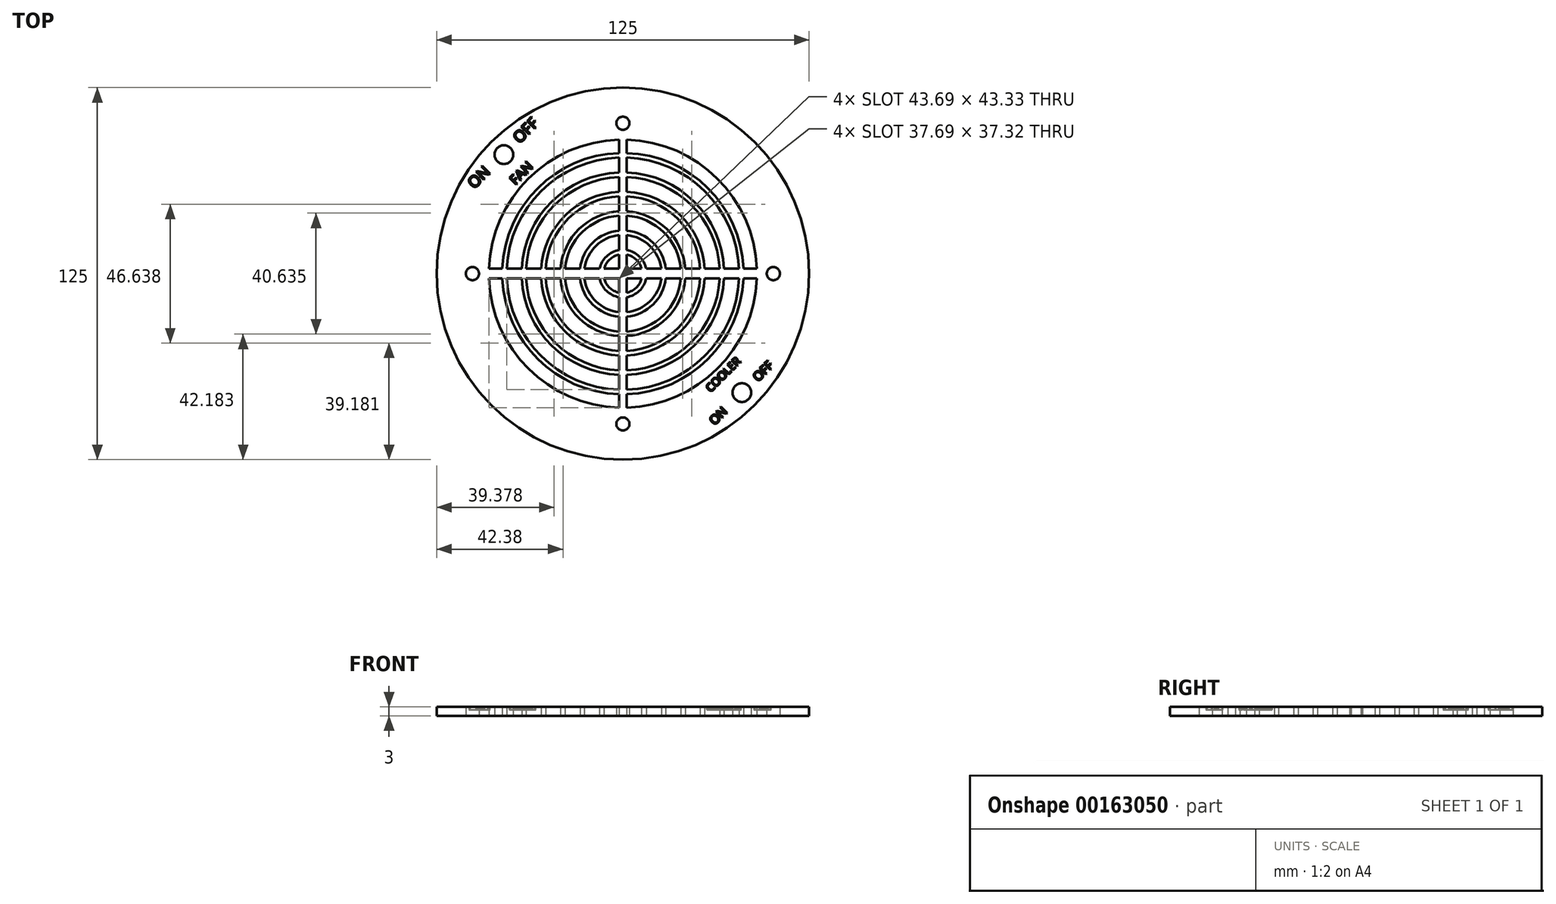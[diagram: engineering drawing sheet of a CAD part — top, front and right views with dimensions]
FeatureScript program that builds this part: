
annotation { "Feature Type Name" : "Feature", "Feature Type Description" : "" }
export const myFeature = defineFeature(function(context is Context, id is Id, definition is map)
    precondition{}
    {
        {
            var Q0;
            Q0=qCreatedBy(makeId("Top.planeOp"),FACE);
            var sketch = newSketch(context, id + "F0", { "sketchPlane" : qUnion([Q0])});
            skArc(sketch, "E0", {"start": v(-44.97, -1.66) * mm, "mid": v(-31.68, -31.95) * mm, "end": v(-1.28, -44.98) * mm});
            skCircle(sketch, "E1", {"center": v(0, 0) * mm, "radius": 62.5 * mm});
            skCircle(sketch, "E2", {"center": v(0, 0) * mm, "radius": 50.5 * mm, "construction": true});
            skPoint(sketch, "E3.center.orphan", {"position": v(-50.5, 0) * mm});
            skPoint(sketch, "E4.center", {"position": v(0.42, -0.72) * mm});
            skPoint(sketch, "E5.start.orphan", {"position": v(0, 45) * mm});
            skPoint(sketch, "E6.start.orphan", {"position": v(0, -45) * mm});
            skPoint(sketch, "E7.orphan", {"position": v(-45, 0) * mm});
            skArc(sketch, "E8", {"start": v(-6.29, -1.66) * mm, "mid": v(-4.46, -4.73) * mm, "end": v(-1.28, -6.37) * mm});
            skArc(sketch, "E9", {"start": v(-7.83, -1.66) * mm, "mid": v(-5.52, -5.8) * mm, "end": v(-1.28, -7.9) * mm});
            skArc(sketch, "E10", {"start": v(-12.9, -1.66) * mm, "mid": v(-9.06, -9.33) * mm, "end": v(-1.28, -12.94) * mm});
            skArc(sketch, "E11", {"start": v(-14.4, -1.66) * mm, "mid": v(-10.12, -10.39) * mm, "end": v(-1.28, -14.44) * mm});
            skArc(sketch, "E12", {"start": v(-19.43, -1.66) * mm, "mid": v(-13.65, -13.92) * mm, "end": v(-1.28, -19.46) * mm});
            skArc(sketch, "E13", {"start": v(-20.93, -1.66) * mm, "mid": v(-14.71, -14.98) * mm, "end": v(-1.28, -20.96) * mm});
            skArc(sketch, "E14", {"start": v(-25.95, -1.66) * mm, "mid": v(-18.25, -18.52) * mm, "end": v(-1.28, -25.97) * mm});
            skArc(sketch, "E15", {"start": v(-27.45, -1.66) * mm, "mid": v(-19.31, -19.58) * mm, "end": v(-1.28, -27.47) * mm});
            skArc(sketch, "E16", {"start": v(-32.46, -1.66) * mm, "mid": v(-22.85, -23.12) * mm, "end": v(-1.28, -32.47) * mm});
            skArc(sketch, "E17", {"start": v(-33.96, -1.66) * mm, "mid": v(-23.9, -24.18) * mm, "end": v(-1.28, -33.98) * mm});
            skArc(sketch, "E18", {"start": v(-38.96, -1.66) * mm, "mid": v(-27.44, -27.71) * mm, "end": v(-1.28, -38.98) * mm});
            skArc(sketch, "E19", {"start": v(-40.47, -1.66) * mm, "mid": v(-28.5, -28.77) * mm, "end": v(-1.28, -40.48) * mm});
            skLineSegment(sketch, "E20.bottom", {"start": v(-44.97, 1.66) * mm, "end": v(-40.47, 1.66) * mm});
            skLineSegment(sketch, "E20.top", {"start": v(-44.97, -1.66) * mm, "end": v(-40.47, -1.66) * mm});
            skLineSegment(sketch, "E21.left", {"start": v(1.28, 44.98) * mm, "end": v(1.28, 40.48) * mm});
            skLineSegment(sketch, "E21.right", {"start": v(-1.28, 44.98) * mm, "end": v(-1.28, 40.48) * mm});
            skPoint(sketch, "E22.orphan", {"position": v(-46.56, 1.66) * mm});
            skPoint(sketch, "E23.orphan", {"position": v(-46.56, -1.66) * mm});
            skLineSegment(sketch, "E24.trimOffspring", {"start": v(-38.96, -1.66) * mm, "end": v(-33.96, -1.66) * mm});
            skLineSegment(sketch, "E25.trimOffspring", {"start": v(-38.96, 1.66) * mm, "end": v(-33.96, 1.66) * mm});
            skLineSegment(sketch, "E26.trimOffspring", {"start": v(-32.46, 1.66) * mm, "end": v(-27.45, 1.66) * mm});
            skLineSegment(sketch, "E27.trimOffspring", {"start": v(-32.46, -1.66) * mm, "end": v(-27.45, -1.66) * mm});
            skLineSegment(sketch, "E28.trimOffspring", {"start": v(-25.95, -1.66) * mm, "end": v(-20.93, -1.66) * mm});
            skLineSegment(sketch, "E29.trimOffspring", {"start": v(-25.95, 1.66) * mm, "end": v(-20.93, 1.66) * mm});
            skLineSegment(sketch, "E30.trimOffspring", {"start": v(-19.43, 1.66) * mm, "end": v(-14.4, 1.66) * mm});
            skLineSegment(sketch, "E31.trimOffspring", {"start": v(-19.43, -1.66) * mm, "end": v(-14.4, -1.66) * mm});
            skLineSegment(sketch, "E32.trimOffspring", {"start": v(-12.9, 1.66) * mm, "end": v(-7.83, 1.66) * mm});
            skLineSegment(sketch, "E33.trimOffspring", {"start": v(-12.9, -1.66) * mm, "end": v(-7.83, -1.66) * mm});
            skLineSegment(sketch, "E34.trimOffspring", {"start": v(-6.29, 1.66) * mm, "end": v(-1.28, 1.66) * mm});
            skLineSegment(sketch, "E35.trimOffspring", {"start": v(-6.29, -1.66) * mm, "end": v(-1.28, -1.66) * mm});
            skLineSegment(sketch, "E36.trimOffspring", {"start": v(-1.28, -1.66) * mm, "end": v(-1.28, -6.37) * mm});
            skLineSegment(sketch, "E37.trimOffspring", {"start": v(1.28, -1.66) * mm, "end": v(1.28, -6.37) * mm});
            skLineSegment(sketch, "E38.trimOffspring", {"start": v(1.28, 1.66) * mm, "end": v(6.29, 1.66) * mm});
            skLineSegment(sketch, "E39.trimOffspring", {"start": v(1.28, -1.66) * mm, "end": v(6.29, -1.66) * mm});
            skArc(sketch, "E40.trimOffspring", {"start": v(-1.28, 6.37) * mm, "mid": v(-4.46, 4.73) * mm, "end": v(-6.29, 1.66) * mm});
            skLineSegment(sketch, "E41.trimOffspring", {"start": v(-1.28, 6.37) * mm, "end": v(-1.28, 1.66) * mm});
            skLineSegment(sketch, "E42.trimOffspring", {"start": v(1.28, 6.37) * mm, "end": v(1.28, 1.66) * mm});
            skArc(sketch, "E43.trimOffspring", {"start": v(-1.28, 12.94) * mm, "mid": v(-9.06, 9.33) * mm, "end": v(-12.9, 1.66) * mm});
            skArc(sketch, "E44.trimOffspring", {"start": v(-1.28, 14.44) * mm, "mid": v(-10.12, 10.39) * mm, "end": v(-14.4, 1.66) * mm});
            skLineSegment(sketch, "E45.trimOffspring", {"start": v(-1.28, 12.94) * mm, "end": v(-1.28, 7.9) * mm});
            skLineSegment(sketch, "E46.trimOffspring", {"start": v(1.28, 12.94) * mm, "end": v(1.28, 7.9) * mm});
            skArc(sketch, "E47.trimOffspring", {"start": v(1.28, -6.37) * mm, "mid": v(4.46, -4.73) * mm, "end": v(6.29, -1.66) * mm});
            skArc(sketch, "E48.trimOffspring", {"start": v(1.28, -7.9) * mm, "mid": v(5.52, -5.8) * mm, "end": v(7.83, -1.66) * mm});
            skLineSegment(sketch, "E49.trimOffspring", {"start": v(1.28, -7.9) * mm, "end": v(1.28, -12.94) * mm});
            skLineSegment(sketch, "E50.trimOffspring", {"start": v(-1.28, -7.9) * mm, "end": v(-1.28, -12.94) * mm});
            skArc(sketch, "E51.trimOffspring", {"start": v(-1.28, 7.9) * mm, "mid": v(-5.52, 5.8) * mm, "end": v(-7.83, 1.66) * mm});
            skArc(sketch, "E52.trimOffspring", {"start": v(-1.28, 19.46) * mm, "mid": v(-13.65, 13.92) * mm, "end": v(-19.43, 1.66) * mm});
            skArc(sketch, "E53.trimOffspring", {"start": v(-1.28, 20.96) * mm, "mid": v(-14.71, 14.98) * mm, "end": v(-20.93, 1.66) * mm});
            skLineSegment(sketch, "E54.trimOffspring", {"start": v(-1.28, 19.46) * mm, "end": v(-1.28, 14.44) * mm});
            skLineSegment(sketch, "E55.trimOffspring", {"start": v(1.28, 19.46) * mm, "end": v(1.28, 14.44) * mm});
            skArc(sketch, "E56.trimOffspring", {"start": v(-1.28, 27.47) * mm, "mid": v(-19.31, 19.58) * mm, "end": v(-27.45, 1.66) * mm});
            skArc(sketch, "E57.trimOffspring", {"start": v(-1.28, 25.97) * mm, "mid": v(-18.25, 18.52) * mm, "end": v(-25.95, 1.66) * mm});
            skLineSegment(sketch, "E58.trimOffspring", {"start": v(-1.28, 25.97) * mm, "end": v(-1.28, 20.96) * mm});
            skLineSegment(sketch, "E59.trimOffspring", {"start": v(1.28, 25.97) * mm, "end": v(1.28, 20.96) * mm});
            skArc(sketch, "E60.trimOffspring", {"start": v(6.29, 1.66) * mm, "mid": v(4.46, 4.73) * mm, "end": v(1.28, 6.37) * mm});
            skArc(sketch, "E61.trimOffspring", {"start": v(7.83, 1.66) * mm, "mid": v(5.52, 5.8) * mm, "end": v(1.28, 7.9) * mm});
            skLineSegment(sketch, "E62.trimOffspring", {"start": v(7.83, 1.66) * mm, "end": v(12.9, 1.66) * mm});
            skLineSegment(sketch, "E63.trimOffspring", {"start": v(7.83, -1.66) * mm, "end": v(12.9, -1.66) * mm});
            skArc(sketch, "E64.trimOffspring", {"start": v(12.9, 1.66) * mm, "mid": v(9.06, 9.33) * mm, "end": v(1.28, 12.94) * mm});
            skArc(sketch, "E65.trimOffspring", {"start": v(14.4, 1.66) * mm, "mid": v(10.12, 10.39) * mm, "end": v(1.28, 14.44) * mm});
            skArc(sketch, "E66.trimOffspring", {"start": v(19.43, 1.66) * mm, "mid": v(13.65, 13.92) * mm, "end": v(1.28, 19.46) * mm});
            skArc(sketch, "E67.trimOffspring", {"start": v(20.93, 1.66) * mm, "mid": v(14.71, 14.98) * mm, "end": v(1.28, 20.96) * mm});
            skArc(sketch, "E68.trimOffspring", {"start": v(25.95, 1.66) * mm, "mid": v(18.25, 18.52) * mm, "end": v(1.28, 25.97) * mm});
            skArc(sketch, "E69.trimOffspring", {"start": v(27.45, 1.66) * mm, "mid": v(19.31, 19.58) * mm, "end": v(1.28, 27.47) * mm});
            skArc(sketch, "E70.trimOffspring", {"start": v(32.46, 1.66) * mm, "mid": v(22.85, 23.12) * mm, "end": v(1.28, 32.47) * mm});
            skArc(sketch, "E71.trimOffspring", {"start": v(33.96, 1.66) * mm, "mid": v(23.9, 24.18) * mm, "end": v(1.28, 33.98) * mm});
            skArc(sketch, "E72.trimOffspring", {"start": v(38.96, 1.66) * mm, "mid": v(27.44, 27.71) * mm, "end": v(1.28, 38.98) * mm});
            skArc(sketch, "E73.trimOffspring", {"start": v(40.47, 1.66) * mm, "mid": v(28.5, 28.77) * mm, "end": v(1.28, 40.48) * mm});
            skPoint(sketch, "E74.orphan", {"position": v(46.56, 1.66) * mm});
            skPoint(sketch, "E75.orphan", {"position": v(46.56, -1.66) * mm});
            skArc(sketch, "E76.trimOffspring", {"start": v(44.97, 1.66) * mm, "mid": v(31.68, 31.95) * mm, "end": v(1.28, 44.98) * mm});
            skLineSegment(sketch, "E77.trimOffspring", {"start": v(40.47, 1.66) * mm, "end": v(44.97, 1.66) * mm});
            skLineSegment(sketch, "E78.trimOffspring", {"start": v(40.47, -1.66) * mm, "end": v(44.97, -1.66) * mm});
            skPoint(sketch, "E79.orphan", {"position": v(-1.28, 46.63) * mm});
            skPoint(sketch, "E80.orphan", {"position": v(1.28, 46.63) * mm});
            skArc(sketch, "E81.trimOffspring", {"start": v(-1.28, 44.98) * mm, "mid": v(-31.68, 31.95) * mm, "end": v(-44.97, 1.66) * mm});
            skArc(sketch, "E82.trimOffspring", {"start": v(-1.28, 40.48) * mm, "mid": v(-28.5, 28.77) * mm, "end": v(-40.47, 1.66) * mm});
            skArc(sketch, "E83.trimOffspring", {"start": v(-1.28, 38.98) * mm, "mid": v(-27.44, 27.71) * mm, "end": v(-38.96, 1.66) * mm});
            skArc(sketch, "E84.trimOffspring", {"start": v(-1.28, 33.98) * mm, "mid": v(-23.9, 24.18) * mm, "end": v(-33.96, 1.66) * mm});
            skArc(sketch, "E85.trimOffspring", {"start": v(-1.28, 32.47) * mm, "mid": v(-22.85, 23.12) * mm, "end": v(-32.46, 1.66) * mm});
            skLineSegment(sketch, "E86.trimOffspring", {"start": v(1.28, 38.98) * mm, "end": v(1.28, 33.98) * mm});
            skLineSegment(sketch, "E87.trimOffspring", {"start": v(-1.28, 38.98) * mm, "end": v(-1.28, 33.98) * mm});
            skLineSegment(sketch, "E88.trimOffspring", {"start": v(-1.28, 32.47) * mm, "end": v(-1.28, 27.47) * mm});
            skLineSegment(sketch, "E89.trimOffspring", {"start": v(1.28, 32.47) * mm, "end": v(1.28, 27.47) * mm});
            skLineSegment(sketch, "E90.trimOffspring", {"start": v(14.4, -1.66) * mm, "end": v(19.43, -1.66) * mm});
            skLineSegment(sketch, "E91.trimOffspring", {"start": v(14.4, 1.66) * mm, "end": v(19.43, 1.66) * mm});
            skLineSegment(sketch, "E92.trimOffspring", {"start": v(20.93, 1.66) * mm, "end": v(25.95, 1.66) * mm});
            skLineSegment(sketch, "E93.trimOffspring", {"start": v(20.93, -1.66) * mm, "end": v(25.95, -1.66) * mm});
            skLineSegment(sketch, "E94.trimOffspring", {"start": v(27.45, 1.66) * mm, "end": v(32.46, 1.66) * mm});
            skLineSegment(sketch, "E95.trimOffspring", {"start": v(27.45, -1.66) * mm, "end": v(32.46, -1.66) * mm});
            skLineSegment(sketch, "E96.trimOffspring", {"start": v(33.96, 1.66) * mm, "end": v(38.96, 1.66) * mm});
            skLineSegment(sketch, "E97.trimOffspring", {"start": v(33.96, -1.66) * mm, "end": v(38.96, -1.66) * mm});
            skArc(sketch, "E98.trimOffspring", {"start": v(1.28, -12.94) * mm, "mid": v(9.06, -9.33) * mm, "end": v(12.9, -1.66) * mm});
            skArc(sketch, "E99.trimOffspring", {"start": v(1.28, -14.44) * mm, "mid": v(10.12, -10.39) * mm, "end": v(14.4, -1.66) * mm});
            skArc(sketch, "E100.trimOffspring", {"start": v(1.28, -19.46) * mm, "mid": v(13.65, -13.92) * mm, "end": v(19.43, -1.66) * mm});
            skArc(sketch, "E101.trimOffspring", {"start": v(1.28, -20.96) * mm, "mid": v(14.71, -14.98) * mm, "end": v(20.93, -1.66) * mm});
            skArc(sketch, "E102.trimOffspring", {"start": v(1.28, -25.97) * mm, "mid": v(18.25, -18.52) * mm, "end": v(25.95, -1.66) * mm});
            skArc(sketch, "E103.trimOffspring", {"start": v(1.28, -27.47) * mm, "mid": v(19.31, -19.58) * mm, "end": v(27.45, -1.66) * mm});
            skArc(sketch, "E104.trimOffspring", {"start": v(1.28, -32.47) * mm, "mid": v(22.85, -23.12) * mm, "end": v(32.46, -1.66) * mm});
            skArc(sketch, "E105.trimOffspring", {"start": v(1.28, -33.98) * mm, "mid": v(23.9, -24.18) * mm, "end": v(33.96, -1.66) * mm});
            skLineSegment(sketch, "E106.trimOffspring", {"start": v(-1.28, -14.44) * mm, "end": v(-1.28, -19.46) * mm});
            skLineSegment(sketch, "E107.trimOffspring", {"start": v(1.28, -14.44) * mm, "end": v(1.28, -19.46) * mm});
            skLineSegment(sketch, "E108.trimOffspring", {"start": v(-1.28, -20.96) * mm, "end": v(-1.28, -25.97) * mm});
            skLineSegment(sketch, "E109.trimOffspring", {"start": v(1.28, -20.96) * mm, "end": v(1.28, -25.97) * mm});
            skLineSegment(sketch, "E110.trimOffspring", {"start": v(-1.28, -27.47) * mm, "end": v(-1.28, -32.47) * mm});
            skLineSegment(sketch, "E111.trimOffspring", {"start": v(1.28, -27.47) * mm, "end": v(1.28, -32.47) * mm});
            skLineSegment(sketch, "E112.trimOffspring", {"start": v(-1.28, -33.98) * mm, "end": v(-1.28, -38.98) * mm});
            skLineSegment(sketch, "E113.trimOffspring", {"start": v(1.28, -33.98) * mm, "end": v(1.28, -38.98) * mm});
            skArc(sketch, "E114.trimOffspring", {"start": v(1.28, -38.98) * mm, "mid": v(27.44, -27.71) * mm, "end": v(38.96, -1.66) * mm});
            skArc(sketch, "E115.trimOffspring", {"start": v(1.28, -40.48) * mm, "mid": v(28.5, -28.77) * mm, "end": v(40.47, -1.66) * mm});
            skLineSegment(sketch, "E116.trimOffspring", {"start": v(-1.28, -40.48) * mm, "end": v(-1.28, -44.98) * mm});
            skLineSegment(sketch, "E117.trimOffspring", {"start": v(1.28, -40.48) * mm, "end": v(1.28, -44.98) * mm});
            skArc(sketch, "E118.trimOffspring", {"start": v(1.28, -44.98) * mm, "mid": v(31.68, -31.95) * mm, "end": v(44.97, -1.66) * mm});
            skPoint(sketch, "E21.top.end.orphan", {"position": v(-1.28, -46.63) * mm});
            skPoint(sketch, "E119.orphan", {"position": v(1.28, -46.63) * mm});
            skCircle(sketch, "E120", {"center": v(0, 0) * mm, "radius": 56.5 * mm, "construction": true});
            skLineSegment(sketch, "E121", {"start": v(-44.2, 44.2) * mm, "end": v(0, 0) * mm, "construction": true});
            skLineSegment(sketch, "E122", {"start": v(0, 0) * mm, "end": v(28.64, -28.64) * mm, "construction": true});
            skLineSegment(sketch, "E123", {"start": v(44.2, -44.2) * mm, "end": v(35.7, -35.7) * mm, "construction": true});
            skLineSegment(sketch, "E124", {"start": v(44.76, 43.62) * mm, "end": v(0.42, -0.72) * mm, "construction": true});
            skLineSegment(sketch, "E125", {"start": v(0, 0) * mm, "end": v(-44.2, -44.2) * mm, "construction": true});
            skPoint(sketch, "E126", {"position": v(-39.95, 39.95) * mm});
            skPoint(sketch, "E127", {"position": v(39.95, -39.95) * mm});
            skPoint(sketch, "E128", {"position": v(0, 50.5) * mm});
            skPoint(sketch, "E129", {"position": v(50.5, 0) * mm});
            skPoint(sketch, "E130", {"position": v(0, -50.5) * mm});
            skLineSegment(sketch, "E131.trimOffspring", {"start": v(31.82, -31.82) * mm, "end": v(0, 0) * mm, "construction": true});
            skLineSegment(sketch, "E132.trimOffspring", {"start": v(35.7, -35.7) * mm, "end": v(44.2, -44.2) * mm, "construction": true});
            skSolve(sketch);
        }
        {
            var Q0;
            Q0 = qSketchRegion(id + "F0", true);
            extrude(context, id + "F1", {"entities" : qUnion([Q0]), "depth" : 3 * mm});
        }
        {
            var Q0;
            Q0=sQuery(id+"F0.wireOp",VERTEX,"E126");
            var Q1;
            Q1=sQuery(id+"F0.wireOp",VERTEX,"E127");
            var Q2;
            Q2=makeQuery(id+"F1.opExtrude","SWEPT_BODY",BODY,{"disambiguationData":[OSD([sQuery(id+"F0.wireOp",EDGE,"E0"),sQuery(id+"F0.wireOp",EDGE,"E1"),sQuery(id+"F0.wireOp",EDGE,"WsTUMAYe-XgrK-ae9x-sZUr-vO0IJ0nvQeYD"),sQuery(id+"F0.wireOp",EDGE,"E4.1.0"),sQuery(id+"F0.wireOp",EDGE,"E4.2.0"),sQuery(id+"F0.wireOp",EDGE,"E4.3.0"),sQuery(id+"F0.wireOp",EDGE,"E8"),sQuery(id+"F0.wireOp",EDGE,"E9"),sQuery(id+"F0.wireOp",EDGE,"E10"),sQuery(id+"F0.wireOp",EDGE,"E11"),sQuery(id+"F0.wireOp",EDGE,"E12"),sQuery(id+"F0.wireOp",EDGE,"E13"),sQuery(id+"F0.wireOp",EDGE,"E14"),sQuery(id+"F0.wireOp",EDGE,"E15"),sQuery(id+"F0.wireOp",EDGE,"E16"),sQuery(id+"F0.wireOp",EDGE,"E17"),sQuery(id+"F0.wireOp",EDGE,"E18"),sQuery(id+"F0.wireOp",EDGE,"E19"),sQuery(id+"F0.wireOp",EDGE,"E20.bottom"),sQuery(id+"F0.wireOp",EDGE,"E20.top"),sQuery(id+"F0.wireOp",EDGE,"E21.left"),sQuery(id+"F0.wireOp",EDGE,"E21.right"),sQuery(id+"F0.wireOp",EDGE,"E24.trimOffspring"),sQuery(id+"F0.wireOp",EDGE,"E25.trimOffspring"),sQuery(id+"F0.wireOp",EDGE,"E26.trimOffspring"),sQuery(id+"F0.wireOp",EDGE,"E27.trimOffspring"),sQuery(id+"F0.wireOp",EDGE,"E28.trimOffspring"),sQuery(id+"F0.wireOp",EDGE,"E29.trimOffspring"),sQuery(id+"F0.wireOp",EDGE,"E30.trimOffspring"),sQuery(id+"F0.wireOp",EDGE,"E31.trimOffspring"),sQuery(id+"F0.wireOp",EDGE,"E32.trimOffspring"),sQuery(id+"F0.wireOp",EDGE,"E33.trimOffspring"),sQuery(id+"F0.wireOp",EDGE,"E34.trimOffspring"),sQuery(id+"F0.wireOp",EDGE,"E35.trimOffspring"),sQuery(id+"F0.wireOp",EDGE,"E36.trimOffspring"),sQuery(id+"F0.wireOp",EDGE,"E37.trimOffspring"),sQuery(id+"F0.wireOp",EDGE,"E38.trimOffspring"),sQuery(id+"F0.wireOp",EDGE,"E39.trimOffspring"),sQuery(id+"F0.wireOp",EDGE,"E40.trimOffspring"),sQuery(id+"F0.wireOp",EDGE,"E41.trimOffspring"),sQuery(id+"F0.wireOp",EDGE,"E42.trimOffspring"),sQuery(id+"F0.wireOp",EDGE,"E43.trimOffspring"),sQuery(id+"F0.wireOp",EDGE,"E44.trimOffspring"),sQuery(id+"F0.wireOp",EDGE,"E45.trimOffspring"),sQuery(id+"F0.wireOp",EDGE,"E46.trimOffspring"),sQuery(id+"F0.wireOp",EDGE,"E47.trimOffspring"),sQuery(id+"F0.wireOp",EDGE,"E48.trimOffspring"),sQuery(id+"F0.wireOp",EDGE,"E49.trimOffspring"),sQuery(id+"F0.wireOp",EDGE,"E50.trimOffspring"),sQuery(id+"F0.wireOp",EDGE,"E51.trimOffspring"),sQuery(id+"F0.wireOp",EDGE,"E52.trimOffspring"),sQuery(id+"F0.wireOp",EDGE,"E53.trimOffspring"),sQuery(id+"F0.wireOp",EDGE,"E54.trimOffspring"),sQuery(id+"F0.wireOp",EDGE,"E55.trimOffspring"),sQuery(id+"F0.wireOp",EDGE,"E56.trimOffspring"),sQuery(id+"F0.wireOp",EDGE,"E57.trimOffspring"),sQuery(id+"F0.wireOp",EDGE,"E58.trimOffspring"),sQuery(id+"F0.wireOp",EDGE,"E59.trimOffspring"),sQuery(id+"F0.wireOp",EDGE,"E60.trimOffspring"),sQuery(id+"F0.wireOp",EDGE,"E61.trimOffspring"),sQuery(id+"F0.wireOp",EDGE,"E62.trimOffspring"),sQuery(id+"F0.wireOp",EDGE,"E63.trimOffspring"),sQuery(id+"F0.wireOp",EDGE,"E64.trimOffspring"),sQuery(id+"F0.wireOp",EDGE,"E65.trimOffspring"),sQuery(id+"F0.wireOp",EDGE,"E66.trimOffspring"),sQuery(id+"F0.wireOp",EDGE,"E67.trimOffspring"),sQuery(id+"F0.wireOp",EDGE,"E68.trimOffspring"),sQuery(id+"F0.wireOp",EDGE,"E69.trimOffspring"),sQuery(id+"F0.wireOp",EDGE,"E70.trimOffspring"),sQuery(id+"F0.wireOp",EDGE,"E71.trimOffspring"),sQuery(id+"F0.wireOp",EDGE,"E72.trimOffspring"),sQuery(id+"F0.wireOp",EDGE,"E73.trimOffspring"),sQuery(id+"F0.wireOp",EDGE,"E76.trimOffspring"),sQuery(id+"F0.wireOp",EDGE,"E77.trimOffspring"),sQuery(id+"F0.wireOp",EDGE,"E78.trimOffspring"),sQuery(id+"F0.wireOp",EDGE,"E81.trimOffspring"),sQuery(id+"F0.wireOp",EDGE,"E82.trimOffspring"),sQuery(id+"F0.wireOp",EDGE,"E83.trimOffspring"),sQuery(id+"F0.wireOp",EDGE,"E84.trimOffspring"),sQuery(id+"F0.wireOp",EDGE,"E85.trimOffspring"),sQuery(id+"F0.wireOp",EDGE,"E86.trimOffspring"),sQuery(id+"F0.wireOp",EDGE,"E87.trimOffspring"),sQuery(id+"F0.wireOp",EDGE,"E88.trimOffspring"),sQuery(id+"F0.wireOp",EDGE,"E89.trimOffspring"),sQuery(id+"F0.wireOp",EDGE,"E90.trimOffspring"),sQuery(id+"F0.wireOp",EDGE,"E91.trimOffspring"),sQuery(id+"F0.wireOp",EDGE,"E92.trimOffspring"),sQuery(id+"F0.wireOp",EDGE,"E93.trimOffspring"),sQuery(id+"F0.wireOp",EDGE,"E94.trimOffspring"),sQuery(id+"F0.wireOp",EDGE,"E95.trimOffspring"),sQuery(id+"F0.wireOp",EDGE,"E96.trimOffspring"),sQuery(id+"F0.wireOp",EDGE,"E97.trimOffspring"),sQuery(id+"F0.wireOp",EDGE,"E98.trimOffspring"),sQuery(id+"F0.wireOp",EDGE,"E99.trimOffspring"),sQuery(id+"F0.wireOp",EDGE,"E100.trimOffspring"),sQuery(id+"F0.wireOp",EDGE,"E101.trimOffspring"),sQuery(id+"F0.wireOp",EDGE,"E102.trimOffspring"),sQuery(id+"F0.wireOp",EDGE,"E103.trimOffspring"),sQuery(id+"F0.wireOp",EDGE,"E104.trimOffspring"),sQuery(id+"F0.wireOp",EDGE,"E105.trimOffspring"),sQuery(id+"F0.wireOp",EDGE,"E106.trimOffspring"),sQuery(id+"F0.wireOp",EDGE,"E107.trimOffspring"),sQuery(id+"F0.wireOp",EDGE,"E108.trimOffspring"),sQuery(id+"F0.wireOp",EDGE,"E109.trimOffspring"),sQuery(id+"F0.wireOp",EDGE,"E110.trimOffspring"),sQuery(id+"F0.wireOp",EDGE,"E111.trimOffspring"),sQuery(id+"F0.wireOp",EDGE,"E112.trimOffspring"),sQuery(id+"F0.wireOp",EDGE,"E113.trimOffspring"),sQuery(id+"F0.wireOp",EDGE,"E114.trimOffspring"),sQuery(id+"F0.wireOp",EDGE,"E115.trimOffspring"),sQuery(id+"F0.wireOp",EDGE,"E116.trimOffspring"),sQuery(id+"F0.wireOp",EDGE,"E117.trimOffspring"),sQuery(id+"F0.wireOp",EDGE,"E118.trimOffspring")])]});
            hole(context, id + "F2", {"style" : HoleStyle.SIMPLE, "endStyle" : HoleEndStyle.BLIND, "oppositeDirection" : true, "holeDiameter" : 6.3 * mm, "holeDepth" : 50 * mm, "locations" : qUnion([Q0, Q1]), "scope" : qUnion([Q2])});
        }
        {
            var Q0;
            Q0=sQuery(id+"F0.wireOp",VERTEX,"E130");
            var Q1;
            Q1=sQuery(id+"F0.wireOp",VERTEX,"E3.center.orphan");
            var Q2;
            Q2=sQuery(id+"F0.wireOp",VERTEX,"E129");
            var Q3;
            Q3=sQuery(id+"F0.wireOp",VERTEX,"E128");
            var Q4;
            Q4=makeQuery(id+"F1.opExtrude","SWEPT_BODY",BODY,{"disambiguationData":[OSD([sQuery(id+"F0.wireOp",EDGE,"E0"),sQuery(id+"F0.wireOp",EDGE,"E1"),sQuery(id+"F0.wireOp",EDGE,"E8"),sQuery(id+"F0.wireOp",EDGE,"E9"),sQuery(id+"F0.wireOp",EDGE,"E10"),sQuery(id+"F0.wireOp",EDGE,"E11"),sQuery(id+"F0.wireOp",EDGE,"E12"),sQuery(id+"F0.wireOp",EDGE,"E13"),sQuery(id+"F0.wireOp",EDGE,"E14"),sQuery(id+"F0.wireOp",EDGE,"E15"),sQuery(id+"F0.wireOp",EDGE,"E16"),sQuery(id+"F0.wireOp",EDGE,"E17"),sQuery(id+"F0.wireOp",EDGE,"E18"),sQuery(id+"F0.wireOp",EDGE,"E19"),sQuery(id+"F0.wireOp",EDGE,"E20.bottom"),sQuery(id+"F0.wireOp",EDGE,"E20.top"),sQuery(id+"F0.wireOp",EDGE,"E21.left"),sQuery(id+"F0.wireOp",EDGE,"E21.right"),sQuery(id+"F0.wireOp",EDGE,"E24.trimOffspring"),sQuery(id+"F0.wireOp",EDGE,"E25.trimOffspring"),sQuery(id+"F0.wireOp",EDGE,"E26.trimOffspring"),sQuery(id+"F0.wireOp",EDGE,"E27.trimOffspring"),sQuery(id+"F0.wireOp",EDGE,"E28.trimOffspring"),sQuery(id+"F0.wireOp",EDGE,"E29.trimOffspring"),sQuery(id+"F0.wireOp",EDGE,"E30.trimOffspring"),sQuery(id+"F0.wireOp",EDGE,"E31.trimOffspring"),sQuery(id+"F0.wireOp",EDGE,"E32.trimOffspring"),sQuery(id+"F0.wireOp",EDGE,"E33.trimOffspring"),sQuery(id+"F0.wireOp",EDGE,"E34.trimOffspring"),sQuery(id+"F0.wireOp",EDGE,"E35.trimOffspring"),sQuery(id+"F0.wireOp",EDGE,"E36.trimOffspring"),sQuery(id+"F0.wireOp",EDGE,"E37.trimOffspring"),sQuery(id+"F0.wireOp",EDGE,"E38.trimOffspring"),sQuery(id+"F0.wireOp",EDGE,"E39.trimOffspring"),sQuery(id+"F0.wireOp",EDGE,"E40.trimOffspring"),sQuery(id+"F0.wireOp",EDGE,"E41.trimOffspring"),sQuery(id+"F0.wireOp",EDGE,"E42.trimOffspring"),sQuery(id+"F0.wireOp",EDGE,"E43.trimOffspring"),sQuery(id+"F0.wireOp",EDGE,"E44.trimOffspring"),sQuery(id+"F0.wireOp",EDGE,"E45.trimOffspring"),sQuery(id+"F0.wireOp",EDGE,"E46.trimOffspring"),sQuery(id+"F0.wireOp",EDGE,"E47.trimOffspring"),sQuery(id+"F0.wireOp",EDGE,"E48.trimOffspring"),sQuery(id+"F0.wireOp",EDGE,"E49.trimOffspring"),sQuery(id+"F0.wireOp",EDGE,"E50.trimOffspring"),sQuery(id+"F0.wireOp",EDGE,"E51.trimOffspring"),sQuery(id+"F0.wireOp",EDGE,"E52.trimOffspring"),sQuery(id+"F0.wireOp",EDGE,"E53.trimOffspring"),sQuery(id+"F0.wireOp",EDGE,"E54.trimOffspring"),sQuery(id+"F0.wireOp",EDGE,"E55.trimOffspring"),sQuery(id+"F0.wireOp",EDGE,"E56.trimOffspring"),sQuery(id+"F0.wireOp",EDGE,"E57.trimOffspring"),sQuery(id+"F0.wireOp",EDGE,"E58.trimOffspring"),sQuery(id+"F0.wireOp",EDGE,"E59.trimOffspring"),sQuery(id+"F0.wireOp",EDGE,"E60.trimOffspring"),sQuery(id+"F0.wireOp",EDGE,"E61.trimOffspring"),sQuery(id+"F0.wireOp",EDGE,"E62.trimOffspring"),sQuery(id+"F0.wireOp",EDGE,"E63.trimOffspring"),sQuery(id+"F0.wireOp",EDGE,"E64.trimOffspring"),sQuery(id+"F0.wireOp",EDGE,"E65.trimOffspring"),sQuery(id+"F0.wireOp",EDGE,"E66.trimOffspring"),sQuery(id+"F0.wireOp",EDGE,"E67.trimOffspring"),sQuery(id+"F0.wireOp",EDGE,"E68.trimOffspring"),sQuery(id+"F0.wireOp",EDGE,"E69.trimOffspring"),sQuery(id+"F0.wireOp",EDGE,"E70.trimOffspring"),sQuery(id+"F0.wireOp",EDGE,"E71.trimOffspring"),sQuery(id+"F0.wireOp",EDGE,"E72.trimOffspring"),sQuery(id+"F0.wireOp",EDGE,"E73.trimOffspring"),sQuery(id+"F0.wireOp",EDGE,"E76.trimOffspring"),sQuery(id+"F0.wireOp",EDGE,"E77.trimOffspring"),sQuery(id+"F0.wireOp",EDGE,"E78.trimOffspring"),sQuery(id+"F0.wireOp",EDGE,"E81.trimOffspring"),sQuery(id+"F0.wireOp",EDGE,"E82.trimOffspring"),sQuery(id+"F0.wireOp",EDGE,"E83.trimOffspring"),sQuery(id+"F0.wireOp",EDGE,"E84.trimOffspring"),sQuery(id+"F0.wireOp",EDGE,"E85.trimOffspring"),sQuery(id+"F0.wireOp",EDGE,"E86.trimOffspring"),sQuery(id+"F0.wireOp",EDGE,"E87.trimOffspring"),sQuery(id+"F0.wireOp",EDGE,"E88.trimOffspring"),sQuery(id+"F0.wireOp",EDGE,"E89.trimOffspring"),sQuery(id+"F0.wireOp",EDGE,"E90.trimOffspring"),sQuery(id+"F0.wireOp",EDGE,"E91.trimOffspring"),sQuery(id+"F0.wireOp",EDGE,"E92.trimOffspring"),sQuery(id+"F0.wireOp",EDGE,"E93.trimOffspring"),sQuery(id+"F0.wireOp",EDGE,"E94.trimOffspring"),sQuery(id+"F0.wireOp",EDGE,"E95.trimOffspring"),sQuery(id+"F0.wireOp",EDGE,"E96.trimOffspring"),sQuery(id+"F0.wireOp",EDGE,"E97.trimOffspring"),sQuery(id+"F0.wireOp",EDGE,"E98.trimOffspring"),sQuery(id+"F0.wireOp",EDGE,"E99.trimOffspring"),sQuery(id+"F0.wireOp",EDGE,"E100.trimOffspring"),sQuery(id+"F0.wireOp",EDGE,"E101.trimOffspring"),sQuery(id+"F0.wireOp",EDGE,"E102.trimOffspring"),sQuery(id+"F0.wireOp",EDGE,"E103.trimOffspring"),sQuery(id+"F0.wireOp",EDGE,"E104.trimOffspring"),sQuery(id+"F0.wireOp",EDGE,"E105.trimOffspring"),sQuery(id+"F0.wireOp",EDGE,"E106.trimOffspring"),sQuery(id+"F0.wireOp",EDGE,"E107.trimOffspring"),sQuery(id+"F0.wireOp",EDGE,"E108.trimOffspring"),sQuery(id+"F0.wireOp",EDGE,"E109.trimOffspring"),sQuery(id+"F0.wireOp",EDGE,"E110.trimOffspring"),sQuery(id+"F0.wireOp",EDGE,"E111.trimOffspring"),sQuery(id+"F0.wireOp",EDGE,"E112.trimOffspring"),sQuery(id+"F0.wireOp",EDGE,"E113.trimOffspring"),sQuery(id+"F0.wireOp",EDGE,"E114.trimOffspring"),sQuery(id+"F0.wireOp",EDGE,"E115.trimOffspring"),sQuery(id+"F0.wireOp",EDGE,"E116.trimOffspring"),sQuery(id+"F0.wireOp",EDGE,"E117.trimOffspring"),sQuery(id+"F0.wireOp",EDGE,"E118.trimOffspring")])]});
            hole(context, id + "F3", {"style" : HoleStyle.SIMPLE, "endStyle" : HoleEndStyle.BLIND, "oppositeDirection" : true, "standardTappedOrClearance" : lookupTablePath({ "standard" : "ISO", "fit" : "Normal", "size" : "M4", "type" : "Clearance" }), "standardBlindInLast" : lookupTablePath({ "fit" : "Standard", "standard" : "ISO", "size" : "M4", "type" : "Clearance" }), "holeDiameter" : 4.4 * mm, "holeDepth" : 50 * mm, "locations" : qUnion([Q0, Q1, Q2, Q3]), "scope" : qUnion([Q4])});
        }
        {
            var Q0;
            Q0=makeQuery(id+"F1.opExtrude","CAP_FACE",FACE,{"disambiguationData":[OSD([sQuery(id+"F0.wireOp",EDGE,"E0"),sQuery(id+"F0.wireOp",EDGE,"E1"),sQuery(id+"F0.wireOp",EDGE,"E8"),sQuery(id+"F0.wireOp",EDGE,"E9"),sQuery(id+"F0.wireOp",EDGE,"E10"),sQuery(id+"F0.wireOp",EDGE,"E11"),sQuery(id+"F0.wireOp",EDGE,"E12"),sQuery(id+"F0.wireOp",EDGE,"E13"),sQuery(id+"F0.wireOp",EDGE,"E14"),sQuery(id+"F0.wireOp",EDGE,"E15"),sQuery(id+"F0.wireOp",EDGE,"E16"),sQuery(id+"F0.wireOp",EDGE,"E17"),sQuery(id+"F0.wireOp",EDGE,"E18"),sQuery(id+"F0.wireOp",EDGE,"E19"),sQuery(id+"F0.wireOp",EDGE,"E20.bottom"),sQuery(id+"F0.wireOp",EDGE,"E20.top"),sQuery(id+"F0.wireOp",EDGE,"E21.left"),sQuery(id+"F0.wireOp",EDGE,"E21.right"),sQuery(id+"F0.wireOp",EDGE,"E24.trimOffspring"),sQuery(id+"F0.wireOp",EDGE,"E25.trimOffspring"),sQuery(id+"F0.wireOp",EDGE,"E26.trimOffspring"),sQuery(id+"F0.wireOp",EDGE,"E27.trimOffspring"),sQuery(id+"F0.wireOp",EDGE,"E28.trimOffspring"),sQuery(id+"F0.wireOp",EDGE,"E29.trimOffspring"),sQuery(id+"F0.wireOp",EDGE,"E30.trimOffspring"),sQuery(id+"F0.wireOp",EDGE,"E31.trimOffspring"),sQuery(id+"F0.wireOp",EDGE,"E32.trimOffspring"),sQuery(id+"F0.wireOp",EDGE,"E33.trimOffspring"),sQuery(id+"F0.wireOp",EDGE,"E34.trimOffspring"),sQuery(id+"F0.wireOp",EDGE,"E35.trimOffspring"),sQuery(id+"F0.wireOp",EDGE,"E36.trimOffspring"),sQuery(id+"F0.wireOp",EDGE,"E37.trimOffspring"),sQuery(id+"F0.wireOp",EDGE,"E38.trimOffspring"),sQuery(id+"F0.wireOp",EDGE,"E39.trimOffspring"),sQuery(id+"F0.wireOp",EDGE,"E40.trimOffspring"),sQuery(id+"F0.wireOp",EDGE,"E41.trimOffspring"),sQuery(id+"F0.wireOp",EDGE,"E42.trimOffspring"),sQuery(id+"F0.wireOp",EDGE,"E43.trimOffspring"),sQuery(id+"F0.wireOp",EDGE,"E44.trimOffspring"),sQuery(id+"F0.wireOp",EDGE,"E45.trimOffspring"),sQuery(id+"F0.wireOp",EDGE,"E46.trimOffspring"),sQuery(id+"F0.wireOp",EDGE,"E47.trimOffspring"),sQuery(id+"F0.wireOp",EDGE,"E48.trimOffspring"),sQuery(id+"F0.wireOp",EDGE,"E49.trimOffspring"),sQuery(id+"F0.wireOp",EDGE,"E50.trimOffspring"),sQuery(id+"F0.wireOp",EDGE,"E51.trimOffspring"),sQuery(id+"F0.wireOp",EDGE,"E52.trimOffspring"),sQuery(id+"F0.wireOp",EDGE,"E53.trimOffspring"),sQuery(id+"F0.wireOp",EDGE,"E54.trimOffspring"),sQuery(id+"F0.wireOp",EDGE,"E55.trimOffspring"),sQuery(id+"F0.wireOp",EDGE,"E56.trimOffspring"),sQuery(id+"F0.wireOp",EDGE,"E57.trimOffspring"),sQuery(id+"F0.wireOp",EDGE,"E58.trimOffspring"),sQuery(id+"F0.wireOp",EDGE,"E59.trimOffspring"),sQuery(id+"F0.wireOp",EDGE,"E60.trimOffspring"),sQuery(id+"F0.wireOp",EDGE,"E61.trimOffspring"),sQuery(id+"F0.wireOp",EDGE,"E62.trimOffspring"),sQuery(id+"F0.wireOp",EDGE,"E63.trimOffspring"),sQuery(id+"F0.wireOp",EDGE,"E64.trimOffspring"),sQuery(id+"F0.wireOp",EDGE,"E65.trimOffspring"),sQuery(id+"F0.wireOp",EDGE,"E66.trimOffspring"),sQuery(id+"F0.wireOp",EDGE,"E67.trimOffspring"),sQuery(id+"F0.wireOp",EDGE,"E68.trimOffspring"),sQuery(id+"F0.wireOp",EDGE,"E69.trimOffspring"),sQuery(id+"F0.wireOp",EDGE,"E70.trimOffspring"),sQuery(id+"F0.wireOp",EDGE,"E71.trimOffspring"),sQuery(id+"F0.wireOp",EDGE,"E72.trimOffspring"),sQuery(id+"F0.wireOp",EDGE,"E73.trimOffspring"),sQuery(id+"F0.wireOp",EDGE,"E76.trimOffspring"),sQuery(id+"F0.wireOp",EDGE,"E77.trimOffspring"),sQuery(id+"F0.wireOp",EDGE,"E78.trimOffspring"),sQuery(id+"F0.wireOp",EDGE,"E81.trimOffspring"),sQuery(id+"F0.wireOp",EDGE,"E82.trimOffspring"),sQuery(id+"F0.wireOp",EDGE,"E83.trimOffspring"),sQuery(id+"F0.wireOp",EDGE,"E84.trimOffspring"),sQuery(id+"F0.wireOp",EDGE,"E85.trimOffspring"),sQuery(id+"F0.wireOp",EDGE,"E86.trimOffspring"),sQuery(id+"F0.wireOp",EDGE,"E87.trimOffspring"),sQuery(id+"F0.wireOp",EDGE,"E88.trimOffspring"),sQuery(id+"F0.wireOp",EDGE,"E89.trimOffspring"),sQuery(id+"F0.wireOp",EDGE,"E90.trimOffspring"),sQuery(id+"F0.wireOp",EDGE,"E91.trimOffspring"),sQuery(id+"F0.wireOp",EDGE,"E92.trimOffspring"),sQuery(id+"F0.wireOp",EDGE,"E93.trimOffspring"),sQuery(id+"F0.wireOp",EDGE,"E94.trimOffspring"),sQuery(id+"F0.wireOp",EDGE,"E95.trimOffspring"),sQuery(id+"F0.wireOp",EDGE,"E96.trimOffspring"),sQuery(id+"F0.wireOp",EDGE,"E97.trimOffspring"),sQuery(id+"F0.wireOp",EDGE,"E98.trimOffspring"),sQuery(id+"F0.wireOp",EDGE,"E99.trimOffspring"),sQuery(id+"F0.wireOp",EDGE,"E100.trimOffspring"),sQuery(id+"F0.wireOp",EDGE,"E101.trimOffspring"),sQuery(id+"F0.wireOp",EDGE,"E102.trimOffspring"),sQuery(id+"F0.wireOp",EDGE,"E103.trimOffspring"),sQuery(id+"F0.wireOp",EDGE,"E104.trimOffspring"),sQuery(id+"F0.wireOp",EDGE,"E105.trimOffspring"),sQuery(id+"F0.wireOp",EDGE,"E106.trimOffspring"),sQuery(id+"F0.wireOp",EDGE,"E107.trimOffspring"),sQuery(id+"F0.wireOp",EDGE,"E108.trimOffspring"),sQuery(id+"F0.wireOp",EDGE,"E109.trimOffspring"),sQuery(id+"F0.wireOp",EDGE,"E110.trimOffspring"),sQuery(id+"F0.wireOp",EDGE,"E111.trimOffspring"),sQuery(id+"F0.wireOp",EDGE,"E112.trimOffspring"),sQuery(id+"F0.wireOp",EDGE,"E113.trimOffspring"),sQuery(id+"F0.wireOp",EDGE,"E114.trimOffspring"),sQuery(id+"F0.wireOp",EDGE,"E115.trimOffspring"),sQuery(id+"F0.wireOp",EDGE,"E116.trimOffspring"),sQuery(id+"F0.wireOp",EDGE,"E117.trimOffspring"),sQuery(id+"F0.wireOp",EDGE,"E118.trimOffspring")])],"isStart":false});
            var sketch = newSketch(context, id + "F4", { "sketchPlane" : qUnion([Q0])});
            skText(sketch, "E133", { "text": "ON          OFF", "fontName": "OpenSans-Regular.ttf"});
            skText(sketch, "E134", { "text": "FAN", "fontName": "OpenSans-Regular.ttf"});
            skText(sketch, "E135", { "text": "COOLER", "fontName": "OpenSans-Regular.ttf"});
            skText(sketch, "E136", { "text": "ON             OFF", "fontName": "OpenSans-Regular.ttf"});
            const initialGuessF4  = {"E133": [-0.04991, 0.0283, 0.7071, 0.7071, 0.00375], "E134": [-0.03609, 0.02952, 0.7071, 0.7071, 0.00334], "E135": [0.02943, -0.03999, 0.7071, 0.7071, 0.00271], "E136": [0.03078, -0.05108, 0.7071, 0.7071, 0.00303]};
            skSetInitialGuess(sketch, initialGuessF4);
            skSolve(sketch);
        }
        {
            var Q0;
            Q0 = qSketchRegion(id + "F4", true);
            extrude(context, id + "F5", {"entities" : qUnion([Q0]), "operationType" : NewBodyOperationType.REMOVE, "oppositeDirection" : true, "depth" : 1 * mm});
        }
    });
